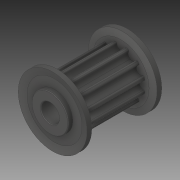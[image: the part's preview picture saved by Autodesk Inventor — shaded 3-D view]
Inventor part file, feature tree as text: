
AUTODESK INVENTOR PART (.ipt)
format: ipt  version: 2019 (Build 230136000, 136)  size: 214,016 bytes
history: native  units: in
note: dims shown in document units (in); Inventor stores cm internally (conversion verified against a paired STEP export)
features: chamfer x1
ambient origin geometry x8: Origin, YZ Plane, XZ Plane, XY Plane, X Axis, Y Axis, Z Axis, Center Point
bodies: Solid1 (feature_tree)
feature tree (1):
  chamfer  "Chamfer1"  [1 undecoded]
note: 1 required parameter value undecoded (feature->parameter linkage not recoverable at this tier; creation-order binding heuristic only, values carry confidence <= 0.55)
